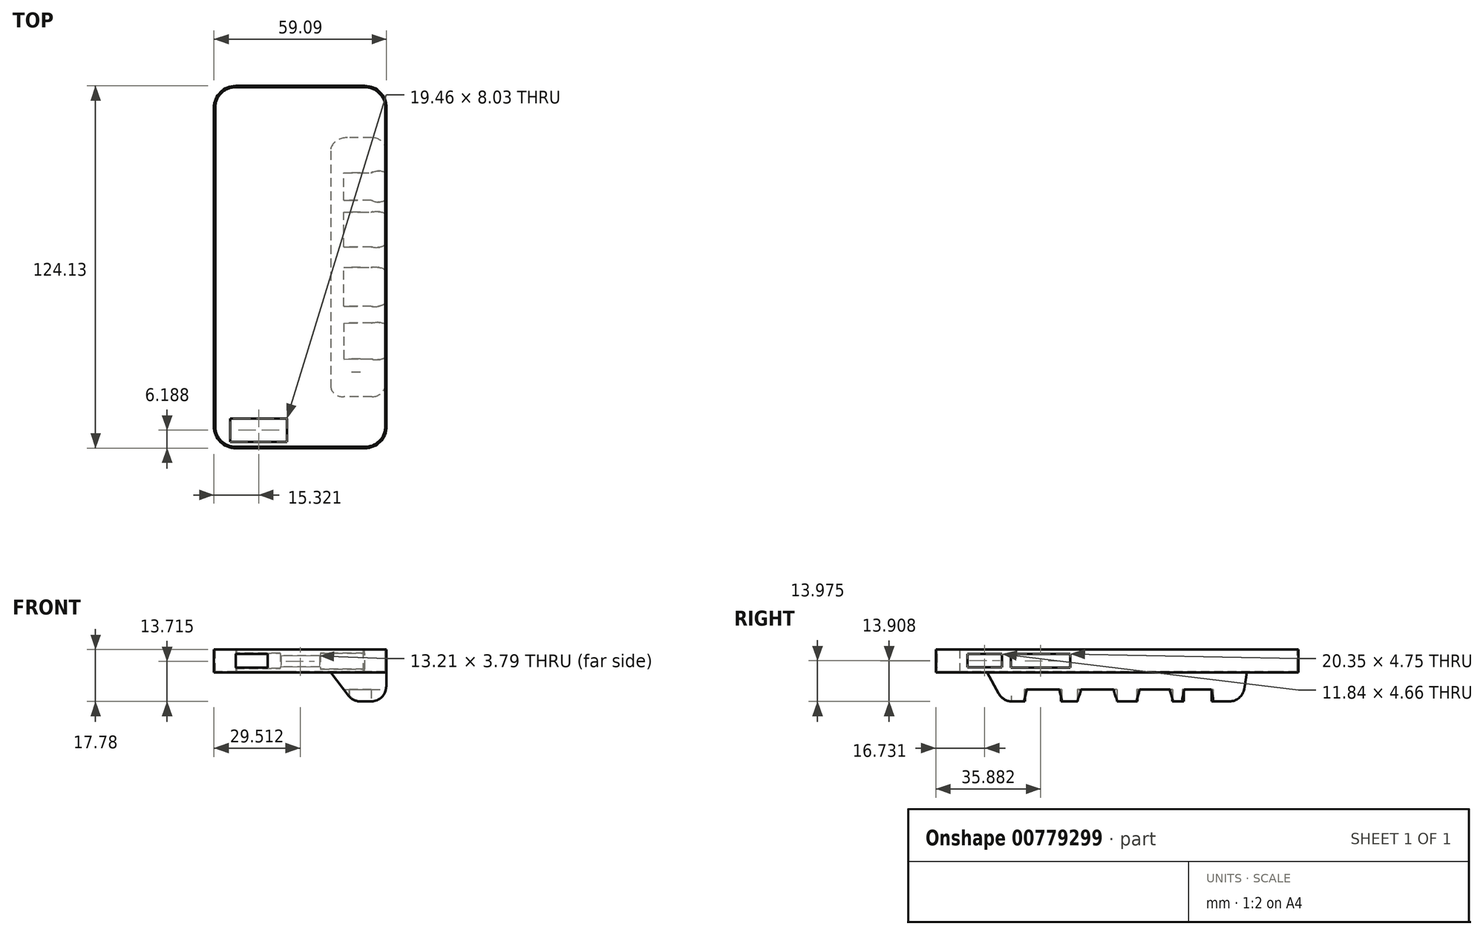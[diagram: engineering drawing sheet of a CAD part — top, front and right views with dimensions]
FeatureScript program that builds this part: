
annotation { "Feature Type Name" : "Feature", "Feature Type Description" : "" }
export const myFeature = defineFeature(function(context is Context, id is Id, definition is map)
    precondition{}
    {
        {
            var Q0;
            Q0=qCreatedBy(makeId("Top.planeOp"),FACE);
            var sketch = newSketch(context, id + "F0", { "sketchPlane" : qUnion([Q0])});
            skLineSegment(sketch, "E0.bottom", {"start": v(-43.7, 51.23) * mm, "end": v(15.4, 51.23) * mm});
            skLineSegment(sketch, "E0.top", {"start": v(-43.7, -72.9) * mm, "end": v(15.4, -72.9) * mm});
            skLineSegment(sketch, "E0.left", {"start": v(-43.7, 51.23) * mm, "end": v(-43.7, -72.9) * mm});
            skLineSegment(sketch, "E0.right", {"start": v(15.4, 51.23) * mm, "end": v(15.4, -72.9) * mm});
            skSolve(sketch);
        }
        {
            var Q0;
            Q0=makeQuery(id+"F0.imprint","IMPRINT",FACE,{"disambiguationData":[TD([[makeQuery(id+"F0.imprint","IMPRINT",EDGE,{"derivedFrom":sQuery(id+"F0.wireOp",EDGE,"E0.bottom")}),-1.0]])]});
            extrude(context, id + "F1", {"entities" : qUnion([Q0]), "depth" : 7.87 * mm, "offsetDistance" : 25.4 * mm});
        }
        {
            var Q0;
            Q0=makeQuery(id+"F1.opExtrude","CAP_FACE",FACE,{"disambiguationData":[OSD([sQuery(id+"F0.wireOp",EDGE,"E0.bottom"),sQuery(id+"F0.wireOp",EDGE,"E0.top"),sQuery(id+"F0.wireOp",EDGE,"E0.left"),sQuery(id+"F0.wireOp",EDGE,"E0.right")])],"isStart":false});
            var sketch = newSketch(context, id + "F2", { "sketchPlane" : qUnion([Q0])});
            skCircle(sketch, "E1", {"center": v(7.97, 43.8) * mm, "radius": 7.43 * mm});
            skCircle(sketch, "E2", {"center": v(-36.26, 43.8) * mm, "radius": 7.43 * mm});
            skCircle(sketch, "E3", {"center": v(-36.26, -65.47) * mm, "radius": 7.43 * mm});
            skCircle(sketch, "E4", {"center": v(7.97, -65.47) * mm, "radius": 7.43 * mm});
            skSolve(sketch);
        }
        {
            var Q0;
            {var subQ0=sQuery(id+"F2.wireOp",EDGE,"E2");var subQ1=makeQuery(id+"F1.opExtrude","CAP_EDGE",EDGE,{"disambiguationData":[OSD([sQuery(id+"F0.wireOp",EDGE,"E0.bottom")])],"isStart":false});var subQ2=makeQuery(id+"F2.imprint","INTERSECT",VERTEX,{"derivedFrom":[subQ1,subQ0]});Q0=makeQuery(id+"F2.imprint","IMPRINT",FACE,{"disambiguationData":[TD([[makeQuery(id+"F2.imprint","IMPRINT",EDGE,{"disambiguationData":[TD([[subQ2,-1.0]])],"derivedFrom":subQ0}),-1.0]])]});}
            var Q1;
            {var subQ0=sQuery(id+"F2.wireOp",EDGE,"E1");var subQ1=makeQuery(id+"F1.opExtrude","CAP_EDGE",EDGE,{"disambiguationData":[OSD([sQuery(id+"F0.wireOp",EDGE,"E0.bottom")])],"isStart":false});var subQ2=makeQuery(id+"F2.imprint","INTERSECT",VERTEX,{"derivedFrom":[subQ1,subQ0]});Q1=makeQuery(id+"F2.imprint","IMPRINT",FACE,{"disambiguationData":[TD([[makeQuery(id+"F2.imprint","IMPRINT",EDGE,{"disambiguationData":[TD([[subQ2,1.0]])],"derivedFrom":subQ0}),-1.0]])]});}
            var Q2;
            {var subQ0=sQuery(id+"F2.wireOp",EDGE,"E4");var subQ1=makeQuery(id+"F1.opExtrude","CAP_EDGE",EDGE,{"disambiguationData":[OSD([sQuery(id+"F0.wireOp",EDGE,"E0.top")])],"isStart":false});var subQ2=makeQuery(id+"F2.imprint","INTERSECT",VERTEX,{"derivedFrom":[subQ1,subQ0]});Q2=makeQuery(id+"F2.imprint","IMPRINT",FACE,{"disambiguationData":[TD([[makeQuery(id+"F2.imprint","IMPRINT",EDGE,{"disambiguationData":[TD([[subQ2,-1.0]])],"derivedFrom":subQ0}),-1.0]])]});}
            var Q3;
            {var subQ0=sQuery(id+"F2.wireOp",EDGE,"E3");var subQ1=makeQuery(id+"F1.opExtrude","CAP_EDGE",EDGE,{"disambiguationData":[OSD([sQuery(id+"F0.wireOp",EDGE,"E0.top")])],"isStart":false});var subQ2=makeQuery(id+"F2.imprint","INTERSECT",VERTEX,{"derivedFrom":[subQ1,subQ0]});Q3=makeQuery(id+"F2.imprint","IMPRINT",FACE,{"disambiguationData":[TD([[makeQuery(id+"F2.imprint","IMPRINT",EDGE,{"disambiguationData":[TD([[subQ2,1.0]])],"derivedFrom":subQ0}),-1.0]])]});}
            extrude(context, id + "F3", {"entities" : qUnion([Q0, Q1, Q2, Q3]), "operationType" : NewBodyOperationType.REMOVE, "oppositeDirection" : true, "depth" : 25.4 * mm, "offsetDistance" : 25.4 * mm});
        }
        {
            var Q0;
            Q0=makeQuery(id+"F1.opExtrude","CAP_FACE",FACE,{"disambiguationData":[OSD([sQuery(id+"F0.wireOp",EDGE,"E0.bottom"),sQuery(id+"F0.wireOp",EDGE,"E0.top"),sQuery(id+"F0.wireOp",EDGE,"E0.left"),sQuery(id+"F0.wireOp",EDGE,"E0.right")])],"isStart":false});
            var sketch = newSketch(context, id + "F4", { "sketchPlane" : qUnion([Q0])});
            skArc(sketch, "E5", {"start": v(-36.14, 50.78) * mm, "mid": v(-41.16, 48.78) * mm, "end": v(-43.25, 43.8) * mm});
            skArc(sketch, "E6", {"start": v(14.96, 43.8) * mm, "mid": v(12.87, 48.78) * mm, "end": v(7.85, 50.78) * mm});
            skArc(sketch, "E7", {"start": v(-43.25, -65.47) * mm, "mid": v(-41.02, -70.58) * mm, "end": v(-35.77, -72.44) * mm});
            skArc(sketch, "E8", {"start": v(7.48, -72.44) * mm, "mid": v(13.03, -70.28) * mm, "end": v(14.9, -64.63) * mm});
            skLineSegment(sketch, "E9", {"start": v(-36.38, 50.78) * mm, "end": v(8.1, 50.78) * mm});
            skLineSegment(sketch, "E10", {"start": v(14.96, 43.8) * mm, "end": v(14.9, -66.32) * mm});
            skLineSegment(sketch, "E11", {"start": v(8.46, -72.44) * mm, "end": v(-36.75, -72.44) * mm});
            skLineSegment(sketch, "E12", {"start": v(-43.25, -65.47) * mm, "end": v(-43.25, 43.8) * mm});
            skSolve(sketch);
        }
        {
            var Q0;
            Q0 = qSketchRegion(id + "F4", true);
            extrude(context, id + "F5", {"entities" : qUnion([Q0]), "operationType" : NewBodyOperationType.REMOVE, "oppositeDirection" : true, "depth" : 7.62 * mm, "offsetDistance" : 25.4 * mm});
        }
        {
            var Q0;
            Q0=makeQuery(id+"F1.opExtrude","CAP_FACE",FACE,{"disambiguationData":[OSD([sQuery(id+"F0.wireOp",EDGE,"E0.bottom"),sQuery(id+"F0.wireOp",EDGE,"E0.top"),sQuery(id+"F0.wireOp",EDGE,"E0.left"),sQuery(id+"F0.wireOp",EDGE,"E0.right")])],"isStart":true});
            var sketch = newSketch(context, id + "F6", { "sketchPlane" : qUnion([Q0])});
            skPoint(sketch, "E13.firstSnap0", {"position": v(-41.52, 70.73) * mm});
            skLineSegment(sketch, "E13.bottom", {"start": v(-38.1, 70.73) * mm, "end": v(-18.64, 70.73) * mm});
            skLineSegment(sketch, "E13.top", {"start": v(-38.1, 62.7) * mm, "end": v(-18.64, 62.7) * mm});
            skLineSegment(sketch, "E13.left", {"start": v(-38.1, 70.73) * mm, "end": v(-38.1, 62.7) * mm});
            skLineSegment(sketch, "E13.right", {"start": v(-18.64, 70.73) * mm, "end": v(-18.64, 62.7) * mm});
            skSolve(sketch);
        }
        {
            var Q0;
            Q0 = qSketchRegion(id + "F6", true);
            extrude(context, id + "F7", {"entities" : qUnion([Q0]), "operationType" : NewBodyOperationType.REMOVE, "oppositeDirection" : true, "depth" : 25.4 * mm, "offsetDistance" : 25.4 * mm});
        }
        {
            var Q0;
            Q0=makeQuery(id+"F1.opExtrude","SWEPT_FACE",FACE,{"disambiguationData":[OSD([sQuery(id+"F0.wireOp",EDGE,"E0.top")])]});
            var sketch = newSketch(context, id + "F8", { "sketchPlane" : qUnion([Q0])});
            skLineSegment(sketch, "E14.bottom", {"start": v(-36.26, 1.7) * mm, "end": v(-25.28, 1.7) * mm});
            skLineSegment(sketch, "E14.top", {"start": v(-36.26, 6.41) * mm, "end": v(-25.28, 6.41) * mm});
            skLineSegment(sketch, "E14.left", {"start": v(-36.26, 1.7) * mm, "end": v(-36.26, 6.41) * mm});
            skLineSegment(sketch, "E14.right", {"start": v(-25.28, 1.7) * mm, "end": v(-25.28, 6.41) * mm});
            skSolve(sketch);
        }
        {
            var Q0;
            Q0 = qSketchRegion(id + "F8", true);
            extrude(context, id + "F9", {"entities" : qUnion([Q0]), "operationType" : NewBodyOperationType.REMOVE, "oppositeDirection" : true, "depth" : 25.4 * mm, "offsetDistance" : 25.4 * mm});
        }
        {
            var Q0;
            Q0=makeQuery(id+"F1.opExtrude","SWEPT_FACE",FACE,{"disambiguationData":[OSD([sQuery(id+"F0.wireOp",EDGE,"E0.right")])]});
            var sketch = newSketch(context, id + "F10", { "sketchPlane" : qUnion([Q0])});
            skLineSegment(sketch, "E15.bottom", {"start": v(-62.1, 6.4) * mm, "end": v(-50.25, 6.4) * mm});
            skLineSegment(sketch, "E15.top", {"start": v(-62.1, 1.74) * mm, "end": v(-50.25, 1.74) * mm});
            skLineSegment(sketch, "E15.left", {"start": v(-62.1, 6.4) * mm, "end": v(-62.1, 1.74) * mm});
            skLineSegment(sketch, "E15.right", {"start": v(-50.25, 6.4) * mm, "end": v(-50.25, 1.74) * mm});
            skSolve(sketch);
        }
        {
            var Q0;
            Q0=makeQuery(id+"F10.imprint","IMPRINT",FACE,{"disambiguationData":[TD([[makeQuery(id+"F10.imprint","IMPRINT",EDGE,{"derivedFrom":sQuery(id+"F10.wireOp",EDGE,"E15.bottom")}),1.0]])]});
            var sketch = newSketch(context, id + "F11", { "sketchPlane" : qUnion([Q0])});
            skLineSegment(sketch, "E16.bottom", {"start": v(-47.2, 6.37) * mm, "end": v(-26.84, 6.37) * mm});
            skLineSegment(sketch, "E16.top", {"start": v(-47.2, 1.62) * mm, "end": v(-26.84, 1.62) * mm});
            skLineSegment(sketch, "E16.left", {"start": v(-47.2, 6.37) * mm, "end": v(-47.2, 1.62) * mm});
            skLineSegment(sketch, "E16.right", {"start": v(-26.84, 6.37) * mm, "end": v(-26.84, 1.62) * mm});
            skSolve(sketch);
        }
        {
            var Q0;
            Q0=makeQuery(id+"F10.imprint","IMPRINT",FACE,{"disambiguationData":[TD([[makeQuery(id+"F10.imprint","IMPRINT",EDGE,{"derivedFrom":sQuery(id+"F10.wireOp",EDGE,"E15.bottom")}),-1.0]])]});
            var Q1;
            Q1=makeQuery(id+"F11.imprint","IMPRINT",FACE,{"disambiguationData":[TD([[makeQuery(id+"F11.imprint","IMPRINT",EDGE,{"derivedFrom":sQuery(id+"F11.wireOp",EDGE,"E16.bottom")}),-1.0]])]});
            extrude(context, id + "F12", {"entities" : qUnion([Q0, Q1]), "operationType" : NewBodyOperationType.REMOVE, "oppositeDirection" : true, "depth" : 25.4 * mm, "offsetDistance" : 25.4 * mm});
        }
        {
            var Q0;
            Q0=makeQuery(id+"F1.opExtrude","SWEPT_FACE",FACE,{"disambiguationData":[OSD([sQuery(id+"F0.wireOp",EDGE,"E0.bottom")])]});
            var sketch = newSketch(context, id + "F13", { "sketchPlane" : qUnion([Q0])});
            skLineSegment(sketch, "E17.bottom", {"start": v(7.57, 5.7) * mm, "end": v(20.78, 5.7) * mm});
            skLineSegment(sketch, "E17.top", {"start": v(7.57, 1.91) * mm, "end": v(20.78, 1.91) * mm});
            skLineSegment(sketch, "E17.left", {"start": v(7.57, 5.7) * mm, "end": v(7.57, 1.91) * mm});
            skLineSegment(sketch, "E17.right", {"start": v(20.78, 5.7) * mm, "end": v(20.78, 1.91) * mm});
            skLineSegment(sketch, "E18.bottom", {"start": v(-7.97, 6.56) * mm, "end": v(7.27, 6.56) * mm});
            skLineSegment(sketch, "E18.top", {"start": v(-7.97, 1.2) * mm, "end": v(7.27, 1.2) * mm});
            skLineSegment(sketch, "E18.left", {"start": v(-7.97, 6.56) * mm, "end": v(-7.97, 1.2) * mm});
            skLineSegment(sketch, "E18.right", {"start": v(7.27, 6.56) * mm, "end": v(7.27, 1.2) * mm});
            skLineSegment(sketch, "E19.bottom", {"start": v(36.26, 6.65) * mm, "end": v(21.02, 6.65) * mm});
            skLineSegment(sketch, "E19.top", {"start": v(36.26, 1.46) * mm, "end": v(21.02, 1.46) * mm});
            skLineSegment(sketch, "E19.left", {"start": v(36.26, 6.65) * mm, "end": v(36.26, 1.46) * mm});
            skLineSegment(sketch, "E19.right", {"start": v(21.02, 6.65) * mm, "end": v(21.02, 1.46) * mm});
            skSolve(sketch);
        }
        {
            var Q0;
            Q0 = qSketchRegion(id + "F13", true);
            extrude(context, id + "F14", {"entities" : qUnion([Q0]), "operationType" : NewBodyOperationType.REMOVE, "oppositeDirection" : true, "depth" : 25.4 * mm, "offsetDistance" : 25.4 * mm});
        }
        {
            var Q0;
            Q0=makeQuery(id+"F1.opExtrude","CAP_FACE",FACE,{"disambiguationData":[OSD([sQuery(id+"F0.wireOp",EDGE,"E0.bottom"),sQuery(id+"F0.wireOp",EDGE,"E0.top"),sQuery(id+"F0.wireOp",EDGE,"E0.left"),sQuery(id+"F0.wireOp",EDGE,"E0.right")])],"isStart":true});
            var sketch = newSketch(context, id + "F15", { "sketchPlane" : qUnion([Q0])});
            skLineSegment(sketch, "E20.bottom", {"start": v(15.4, -33.53) * mm, "end": v(-3.77, -33.53) * mm});
            skLineSegment(sketch, "E20.top", {"start": v(15.4, 55.3) * mm, "end": v(-3.77, 55.3) * mm});
            skLineSegment(sketch, "E20.left", {"start": v(15.4, -33.53) * mm, "end": v(15.4, 55.3) * mm});
            skLineSegment(sketch, "E20.right", {"start": v(-3.77, -33.53) * mm, "end": v(-3.77, 55.3) * mm});
            skSolve(sketch);
        }
        {
            var Q0;
            Q0=qCreatedBy(makeId("Top.planeOp"),FACE);
            cPlane(context, id + "F16", {"entities" : qUnion([Q0]), "cplaneType" : CPlaneType.OFFSET, "offset" : 9.9 * mm, "oppositeDirection" : true, "width" : 152.4 * mm, "height" : 152.4 * mm});
        }
        {
            var Q0;
            Q0=qCreatedBy(id+"F16.planeOp",FACE);
            var sketch = newSketch(context, id + "F17", { "sketchPlane" : qUnion([Q0])});
            skLineSegment(sketch, "E21.bottom", {"start": v(15.15, 31.9) * mm, "end": v(3.94, 31.9) * mm});
            skLineSegment(sketch, "E21.top", {"start": v(15.15, -49.95) * mm, "end": v(3.94, -49.95) * mm});
            skLineSegment(sketch, "E21.left", {"start": v(15.15, 31.9) * mm, "end": v(15.15, -49.95) * mm});
            skLineSegment(sketch, "E21.right", {"start": v(3.94, 31.9) * mm, "end": v(3.94, -49.95) * mm});
            skSolve(sketch);
        }
        {
            var Q1;
            Q1=makeQuery(id+"F15.imprint","IMPRINT",FACE,{"disambiguationData":[TD([[makeQuery(id+"F15.imprint","IMPRINT",EDGE,{"derivedFrom":sQuery(id+"F15.wireOp",EDGE,"E20.bottom")}),-1.0]])]});
            var Q2;
            Q2=makeQuery(id+"F17.imprint","IMPRINT",FACE,{"disambiguationData":[TD([[makeQuery(id+"F17.imprint","IMPRINT",EDGE,{"derivedFrom":sQuery(id+"F17.wireOp",EDGE,"E21.bottom")}),1.0]])]});
            loft(context, id + "F18", {"operationType" : NewBodyOperationType.ADD, "sheetProfilesArray" : [{ "sheetProfileEntities" : qUnion([Q1]) }, { "sheetProfileEntities" : qUnion([Q2]) }]});
        }
        {
            var Q0;
            Q0=makeQuery(id+"F18.opLoft","MID_CAP_EDGE",EDGE,{"disambiguationData":[OSD([sQuery(id+"F17.wireOp",EDGE,"E21.bottom"),sQuery(id+"F17.wireOp",EDGE,"E21.top"),sQuery(id+"F17.wireOp",EDGE,"E21.right")])],"capPos":1.0});
            fillet(context, id + "F19", {"entities" : qUnion([Q0]), "radius" : 5.08 * mm, "tangentPropagation" : true, "allowEdgeOverflow" : false});
        }
        {
            var Q0;
            Q0=makeQuery(id+"F18.opLoft","SWEPT_EDGE",EDGE,{"disambiguationData":[OSD([sQuery(id+"F15.wireOp",EDGE,"E20.bottom"),sQuery(id+"F15.wireOp",EDGE,"E20.right"),sQuery(id+"F17.wireOp",EDGE,"E21.bottom"),sQuery(id+"F17.wireOp",EDGE,"E21.right")])]});
            var Q1;
            Q1=makeQuery(id+"F18.opLoft","MID_CAP_EDGE",EDGE,{"disambiguationData":[OSD([sQuery(id+"F17.wireOp",EDGE,"E21.bottom"),sQuery(id+"F17.wireOp",EDGE,"E21.left"),sQuery(id+"F17.wireOp",EDGE,"E21.right")])],"capPos":1.0});
            var Q2;
            {var subQ0=sQuery(id+"F17.wireOp",EDGE,"E21.right");var subQ1=sQuery(id+"F17.wireOp",EDGE,"E21.bottom");Q2=makeQuery(id+"F19.opFillet","BLEND_EDGE",EDGE,{"blendedFrom":[makeQuery(id+"F18.opLoft","MID_CAP_EDGE",EDGE,{"disambiguationData":[OSD([subQ1,sQuery(id+"F17.wireOp",EDGE,"E21.top"),subQ0])],"capPos":1.0}),makeQuery(id+"F18.opLoft","SWEPT_FACE",FACE,{"disambiguationData":[OSD([sQuery(id+"F0.wireOp",EDGE,"E0.right"),sQuery(id+"F15.wireOp",EDGE,"E20.bottom"),sQuery(id+"F15.wireOp",EDGE,"E20.left"),sQuery(id+"F15.wireOp",EDGE,"E20.right"),subQ1,sQuery(id+"F17.wireOp",EDGE,"E21.left"),subQ0])]})],"blendedInto":[makeQuery(id+"F18.opLoft","SWEPT_FACE",FACE,{"disambiguationData":[OSD([sQuery(id+"F0.wireOp",EDGE,"E0.right"),sQuery(id+"F15.wireOp",EDGE,"E20.bottom"),sQuery(id+"F15.wireOp",EDGE,"E20.left"),sQuery(id+"F15.wireOp",EDGE,"E20.right"),subQ1,sQuery(id+"F17.wireOp",EDGE,"E21.left"),subQ0])]})]});}
            fillet(context, id + "F20", {"entities" : qUnion([Q0, Q1, Q2]), "radius" : 5.08 * mm, "tangentPropagation" : true, "allowEdgeOverflow" : false});
        }
        {
            var Q0;
            Q0=makeQuery(id+"F18.opLoft","MID_CAP_EDGE",EDGE,{"disambiguationData":[OSD([sQuery(id+"F17.wireOp",EDGE,"E21.top"),sQuery(id+"F17.wireOp",EDGE,"E21.left"),sQuery(id+"F17.wireOp",EDGE,"E21.right")])],"capPos":1.0});
            var Q1;
            Q1=makeQuery(id+"F18.opLoft","SWEPT_EDGE",EDGE,{"disambiguationData":[OSD([sQuery(id+"F15.wireOp",EDGE,"E20.top"),sQuery(id+"F15.wireOp",EDGE,"E20.right"),sQuery(id+"F17.wireOp",EDGE,"E21.top"),sQuery(id+"F17.wireOp",EDGE,"E21.right")])]});
            var Q2;
            {var subQ0=sQuery(id+"F17.wireOp",EDGE,"E21.right");var subQ1=sQuery(id+"F17.wireOp",EDGE,"E21.top");Q2=makeQuery(id+"F19.opFillet","BLEND_EDGE",EDGE,{"blendedFrom":[makeQuery(id+"F18.opLoft","MID_CAP_EDGE",EDGE,{"disambiguationData":[OSD([sQuery(id+"F17.wireOp",EDGE,"E21.bottom"),subQ1,subQ0])],"capPos":1.0}),makeQuery(id+"F18.opLoft","SWEPT_FACE",FACE,{"disambiguationData":[OSD([sQuery(id+"F0.wireOp",EDGE,"E0.right"),sQuery(id+"F15.wireOp",EDGE,"E20.top"),sQuery(id+"F15.wireOp",EDGE,"E20.left"),sQuery(id+"F15.wireOp",EDGE,"E20.right"),subQ1,sQuery(id+"F17.wireOp",EDGE,"E21.left"),subQ0])]})],"blendedInto":[makeQuery(id+"F18.opLoft","SWEPT_FACE",FACE,{"disambiguationData":[OSD([sQuery(id+"F0.wireOp",EDGE,"E0.right"),sQuery(id+"F15.wireOp",EDGE,"E20.top"),sQuery(id+"F15.wireOp",EDGE,"E20.left"),sQuery(id+"F15.wireOp",EDGE,"E20.right"),subQ1,sQuery(id+"F17.wireOp",EDGE,"E21.left"),subQ0])]})]});}
            fillet(context, id + "F21", {"entities" : qUnion([Q0, Q1, Q2]), "radius" : 5.08 * mm, "tangentPropagation" : true, "allowEdgeOverflow" : false});
        }
        {
            var Q0;
            {var subQ0=sQuery(id+"F17.wireOp",EDGE,"E21.left");var subQ1=sQuery(id+"F17.wireOp",EDGE,"E21.bottom");Q0=makeQuery(id+"F20.opFillet","BLEND_EDGE",EDGE,{"blendedFrom":[makeQuery(id+"F18.opLoft","MID_CAP_EDGE",EDGE,{"disambiguationData":[OSD([subQ1,subQ0,sQuery(id+"F17.wireOp",EDGE,"E21.right")])],"capPos":1.0}),makeQuery(id+"F18.opLoft","SWEPT_FACE",FACE,{"disambiguationData":[OSD([sQuery(id+"F0.wireOp",EDGE,"E0.right"),sQuery(id+"F15.wireOp",EDGE,"E20.bottom"),sQuery(id+"F15.wireOp",EDGE,"E20.top"),sQuery(id+"F15.wireOp",EDGE,"E20.left"),subQ1,sQuery(id+"F17.wireOp",EDGE,"E21.top"),subQ0])]})],"blendedInto":[makeQuery(id+"F18.opLoft","SWEPT_FACE",FACE,{"disambiguationData":[OSD([sQuery(id+"F0.wireOp",EDGE,"E0.right"),sQuery(id+"F15.wireOp",EDGE,"E20.bottom"),sQuery(id+"F15.wireOp",EDGE,"E20.top"),sQuery(id+"F15.wireOp",EDGE,"E20.left"),subQ1,sQuery(id+"F17.wireOp",EDGE,"E21.top"),subQ0])]})]});}
            var Q1;
            Q1=makeQuery(id+"F18.opLoft","SWEPT_EDGE",EDGE,{"disambiguationData":[OSD([sQuery(id+"F0.wireOp",EDGE,"E0.right"),sQuery(id+"F15.wireOp",EDGE,"E20.bottom"),sQuery(id+"F15.wireOp",EDGE,"E20.left"),sQuery(id+"F17.wireOp",EDGE,"E21.bottom"),sQuery(id+"F17.wireOp",EDGE,"E21.left")])]});
            var Q2;
            {var subQ0=sQuery(id+"F17.wireOp",EDGE,"E21.left");var subQ1=sQuery(id+"F17.wireOp",EDGE,"E21.top");var subQ2=sQuery(id+"F17.wireOp",EDGE,"E21.bottom");var subQ3=sQuery(id+"F15.wireOp",EDGE,"E20.left");var subQ4=sQuery(id+"F15.wireOp",EDGE,"E20.bottom");var subQ5=sQuery(id+"F0.wireOp",EDGE,"E0.right");var subQ6=sQuery(id+"F17.wireOp",EDGE,"E21.right");Q2=makeQuery(id+"FEJ2AXNtqdchjc9_1.boolean.opBoolean","SPLIT",EDGE,{"disambiguationData":[TD([makeQuery(id+"F18.opLoft","SWEPT_FACE",FACE,{"disambiguationData":[OSD([subQ5,subQ4,subQ3,sQuery(id+"F15.wireOp",EDGE,"E20.right"),subQ2,subQ0,subQ6])]}),makeQuery(id+"F18.opLoft","SWEPT_FACE",FACE,{"disambiguationData":[OSD([subQ5,subQ4,sQuery(id+"F15.wireOp",EDGE,"E20.top"),subQ3,subQ2,subQ1,subQ0])]}),makeQuery(id+"F18.opLoft","CAP_FACE",FACE,{"disambiguationData":[OSD([makeQuery(id+"F17.imprint","IMPRINT",FACE,{"disambiguationData":[TD([[makeQuery(id+"F17.imprint","IMPRINT",EDGE,{"derivedFrom":subQ2}),1.0]])]})])],"isStart":true}),makeQuery(id+"FEJ2AXNtqdchjc9_1.opExtrude","SWEPT_FACE",FACE,{"disambiguationData":[OSD([sQuery(id+"FDW1x2Lz0C1XZF6_1.wireOp",EDGE,"JanS8ljC-JfCv-pVl7-kBYy-5y3HXVbc28N6")])]}),makeQuery(id+"FEJ2AXNtqdchjc9_1.opExtrude","SWEPT_FACE",FACE,{"disambiguationData":[OSD([sQuery(id+"FDW1x2Lz0C1XZF6_1.wireOp",EDGE,"D3cbwERx-BYdt-rjvu-CNmb-xadvX1WlsaeP")])]})])],"derivedFrom":makeQuery(id+"F18.opLoft","MID_CAP_EDGE",EDGE,{"disambiguationData":[OSD([subQ2,subQ1,subQ0])],"capPos":1.0})});}
            var Q3;
            {var subQ0=sQuery(id+"F17.wireOp",EDGE,"E21.left");var subQ1=sQuery(id+"F17.wireOp",EDGE,"E21.top");Q3=makeQuery(id+"F21.opFillet","BLEND_EDGE",EDGE,{"blendedFrom":[makeQuery(id+"F18.opLoft","MID_CAP_EDGE",EDGE,{"disambiguationData":[OSD([subQ1,subQ0,sQuery(id+"F17.wireOp",EDGE,"E21.right")])],"capPos":1.0}),makeQuery(id+"F18.opLoft","SWEPT_FACE",FACE,{"disambiguationData":[OSD([sQuery(id+"F0.wireOp",EDGE,"E0.right"),sQuery(id+"F15.wireOp",EDGE,"E20.bottom"),sQuery(id+"F15.wireOp",EDGE,"E20.top"),sQuery(id+"F15.wireOp",EDGE,"E20.left"),sQuery(id+"F17.wireOp",EDGE,"E21.bottom"),subQ1,subQ0])]})],"blendedInto":[makeQuery(id+"F18.opLoft","SWEPT_FACE",FACE,{"disambiguationData":[OSD([sQuery(id+"F0.wireOp",EDGE,"E0.right"),sQuery(id+"F15.wireOp",EDGE,"E20.bottom"),sQuery(id+"F15.wireOp",EDGE,"E20.top"),sQuery(id+"F15.wireOp",EDGE,"E20.left"),sQuery(id+"F17.wireOp",EDGE,"E21.bottom"),subQ1,subQ0])]})]});}
            var Q4;
            Q4=makeQuery(id+"F18.opLoft","SWEPT_EDGE",EDGE,{"disambiguationData":[OSD([sQuery(id+"F0.wireOp",EDGE,"E0.right"),sQuery(id+"F15.wireOp",EDGE,"E20.top"),sQuery(id+"F15.wireOp",EDGE,"E20.left"),sQuery(id+"F17.wireOp",EDGE,"E21.top"),sQuery(id+"F17.wireOp",EDGE,"E21.left")])]});
            fillet(context, id + "F22", {"entities" : qUnion([Q0, Q1, Q2, Q3, Q4]), "radius" : 5.08 * mm, "tangentPropagation" : true, "allowEdgeOverflow" : false});
        }
        {
            var Q0;
            Q0=makeQuery(id+"F18.opLoft","CAP_FACE",FACE,{"disambiguationData":[OSD([makeQuery(id+"F17.imprint","IMPRINT",FACE,{"disambiguationData":[TD([[makeQuery(id+"F17.imprint","IMPRINT",EDGE,{"derivedFrom":sQuery(id+"F17.wireOp",EDGE,"E21.bottom")}),1.0]])]})])],"isStart":true});
            var sketch = newSketch(context, id + "F23", { "sketchPlane" : qUnion([Q0])});
            skLineSegment(sketch, "E22", {"start": v(2.7, 42.35) * mm, "end": v(10.2, 42.35) * mm});
            skLineSegment(sketch, "E23", {"start": v(10.2, 30.06) * mm, "end": v(2.47, 30.06) * mm});
            skLineSegment(sketch, "E24", {"start": v(2.47, 30.06) * mm, "end": v(2.7, 42.35) * mm});
            skLineSegment(sketch, "E25", {"start": v(10.2, 24.34) * mm, "end": v(2.7, 24.34) * mm});
            skLineSegment(sketch, "E26", {"start": v(2.7, 24.34) * mm, "end": v(2.7, 10.93) * mm});
            skLineSegment(sketch, "E27", {"start": v(2.7, 10.93) * mm, "end": v(10.2, 10.93) * mm});
            skLineSegment(sketch, "E28", {"start": v(10.2, 3.93) * mm, "end": v(2.7, 3.93) * mm});
            skLineSegment(sketch, "E29", {"start": v(2.7, 3.93) * mm, "end": v(2.7, -7.97) * mm});
            skLineSegment(sketch, "E30", {"start": v(2.7, -7.97) * mm, "end": v(10.2, -7.97) * mm});
            skLineSegment(sketch, "E31", {"start": v(10.2, -11.99) * mm, "end": v(2.7, -11.99) * mm});
            skLineSegment(sketch, "E32", {"start": v(2.7, -11.99) * mm, "end": v(2.7, -21.5) * mm});
            skLineSegment(sketch, "E33", {"start": v(2.7, -21.5) * mm, "end": v(10.2, -21.5) * mm});
            skArc(sketch, "E34", {"start": v(10.2, 30.06) * mm, "mid": v(18.49, 36.2) * mm, "end": v(10.2, 42.35) * mm});
            skArc(sketch, "E35", {"start": v(10.2, 10.93) * mm, "mid": v(18.16, 17.63) * mm, "end": v(10.2, 24.34) * mm});
            skArc(sketch, "E36", {"start": v(10.2, -7.97) * mm, "mid": v(18.02, -2.02) * mm, "end": v(10.2, 3.93) * mm});
            skArc(sketch, "E37", {"start": v(10.2, -21.5) * mm, "mid": v(17.92, -16.74) * mm, "end": v(10.2, -11.99) * mm});
            skSolve(sketch);
        }
        {
            var Q0;
            Q0 = qSketchRegion(id + "F23", true);
            extrude(context, id + "F24", {"entities" : qUnion([Q0]), "operationType" : NewBodyOperationType.REMOVE, "oppositeDirection" : true, "depth" : 4.06 * mm, "offsetDistance" : 25.4 * mm});
        }
        {
            var Q0;
            Q0=makeQuery(id+"F24.boolean.opBoolean","COPY",FACE,{"derivedFrom":makeQuery(id+"F24.opExtrude","SWEPT_FACE",FACE,{"disambiguationData":[OSD([sQuery(id+"F23.wireOp",EDGE,"E32")])]})});
            var sketch = newSketch(context, id + "F25", { "sketchPlane" : qUnion([Q0])});
            skLineSegment(sketch, "E38", {"start": v(21.5, -8.28) * mm, "end": v(21.5, -5.84) * mm});
            skLineSegment(sketch, "E39", {"start": v(21.5, -5.84) * mm, "end": v(11.99, -5.84) * mm});
            skLineSegment(sketch, "E40", {"start": v(11.99, -5.84) * mm, "end": v(11.99, -8.28) * mm});
            skLineSegment(sketch, "E41", {"start": v(11.99, -8.28) * mm, "end": v(21.5, -8.28) * mm});
            skSolve(sketch);
        }
        {
            var Q0;
            Q0 = qSketchRegion(id + "F25", true);
            extrude(context, id + "F26", {"entities" : qUnion([Q0]), "operationType" : NewBodyOperationType.REMOVE, "oppositeDirection" : true, "depth" : 25.4 * mm, "offsetDistance" : 25.4 * mm});
        }
        {
            var Q0;
            Q0=makeQuery(id+"F24.boolean.opBoolean","COPY",FACE,{"derivedFrom":makeQuery(id+"F24.opExtrude","SWEPT_FACE",FACE,{"disambiguationData":[OSD([sQuery(id+"F23.wireOp",EDGE,"E29")])]})});
            var sketch = newSketch(context, id + "F27", { "sketchPlane" : qUnion([Q0])});
            skLineSegment(sketch, "E42", {"start": v(7.97, -8.28) * mm, "end": v(7.97, -5.84) * mm});
            skLineSegment(sketch, "E43", {"start": v(7.97, -5.84) * mm, "end": v(-3.93, -5.84) * mm});
            skLineSegment(sketch, "E44", {"start": v(-3.93, -5.84) * mm, "end": v(-3.93, -8.28) * mm});
            skLineSegment(sketch, "E45", {"start": v(-3.93, -8.28) * mm, "end": v(7.97, -8.28) * mm});
            skSolve(sketch);
        }
        {
            var Q0;
            Q0 = qSketchRegion(id + "F27", true);
            extrude(context, id + "F28", {"entities" : qUnion([Q0]), "operationType" : NewBodyOperationType.REMOVE, "oppositeDirection" : true, "depth" : 25.4 * mm, "offsetDistance" : 25.4 * mm});
        }
        {
            var Q0;
            Q0=makeQuery(id+"F24.boolean.opBoolean","COPY",FACE,{"derivedFrom":makeQuery(id+"F24.opExtrude","SWEPT_FACE",FACE,{"disambiguationData":[OSD([sQuery(id+"F23.wireOp",EDGE,"E26")])]})});
            var sketch = newSketch(context, id + "F29", { "sketchPlane" : qUnion([Q0])});
            skLineSegment(sketch, "E46", {"start": v(-10.93, -8.28) * mm, "end": v(-10.93, -5.84) * mm});
            skLineSegment(sketch, "E47", {"start": v(-10.93, -5.84) * mm, "end": v(-24.34, -5.84) * mm});
            skLineSegment(sketch, "E48", {"start": v(-24.34, -5.84) * mm, "end": v(-24.34, -8.28) * mm});
            skLineSegment(sketch, "E49", {"start": v(-24.34, -8.28) * mm, "end": v(-10.93, -8.28) * mm});
            skSolve(sketch);
        }
        {
            var Q0;
            Q0 = qSketchRegion(id + "F29", true);
            extrude(context, id + "F30", {"entities" : qUnion([Q0]), "operationType" : NewBodyOperationType.REMOVE, "oppositeDirection" : true, "depth" : 25.4 * mm, "offsetDistance" : 25.4 * mm});
        }
        {
            var Q0;
            Q0=makeQuery(id+"F24.boolean.opBoolean","COPY",FACE,{"derivedFrom":makeQuery(id+"F24.opExtrude","SWEPT_FACE",FACE,{"disambiguationData":[OSD([sQuery(id+"F23.wireOp",EDGE,"E24")])]})});
            var sketch = newSketch(context, id + "F31", { "sketchPlane" : qUnion([Q0])});
            skLineSegment(sketch, "E50", {"start": v(-30.1, -8.02) * mm, "end": v(-30.1, -5.84) * mm});
            skLineSegment(sketch, "E51", {"start": v(-30.1, -5.84) * mm, "end": v(-42.4, -5.84) * mm});
            skLineSegment(sketch, "E52", {"start": v(-42.4, -5.84) * mm, "end": v(-42.4, -8.28) * mm});
            skLineSegment(sketch, "E53", {"start": v(-42.4, -8.28) * mm, "end": v(-30.1, -8.02) * mm});
            skSolve(sketch);
        }
        {
            var Q0;
            Q0 = qSketchRegion(id + "F31", true);
            extrude(context, id + "F32", {"entities" : qUnion([Q0]), "operationType" : NewBodyOperationType.REMOVE, "oppositeDirection" : true, "depth" : 25.4 * mm, "offsetDistance" : 25.4 * mm});
        }
    });
